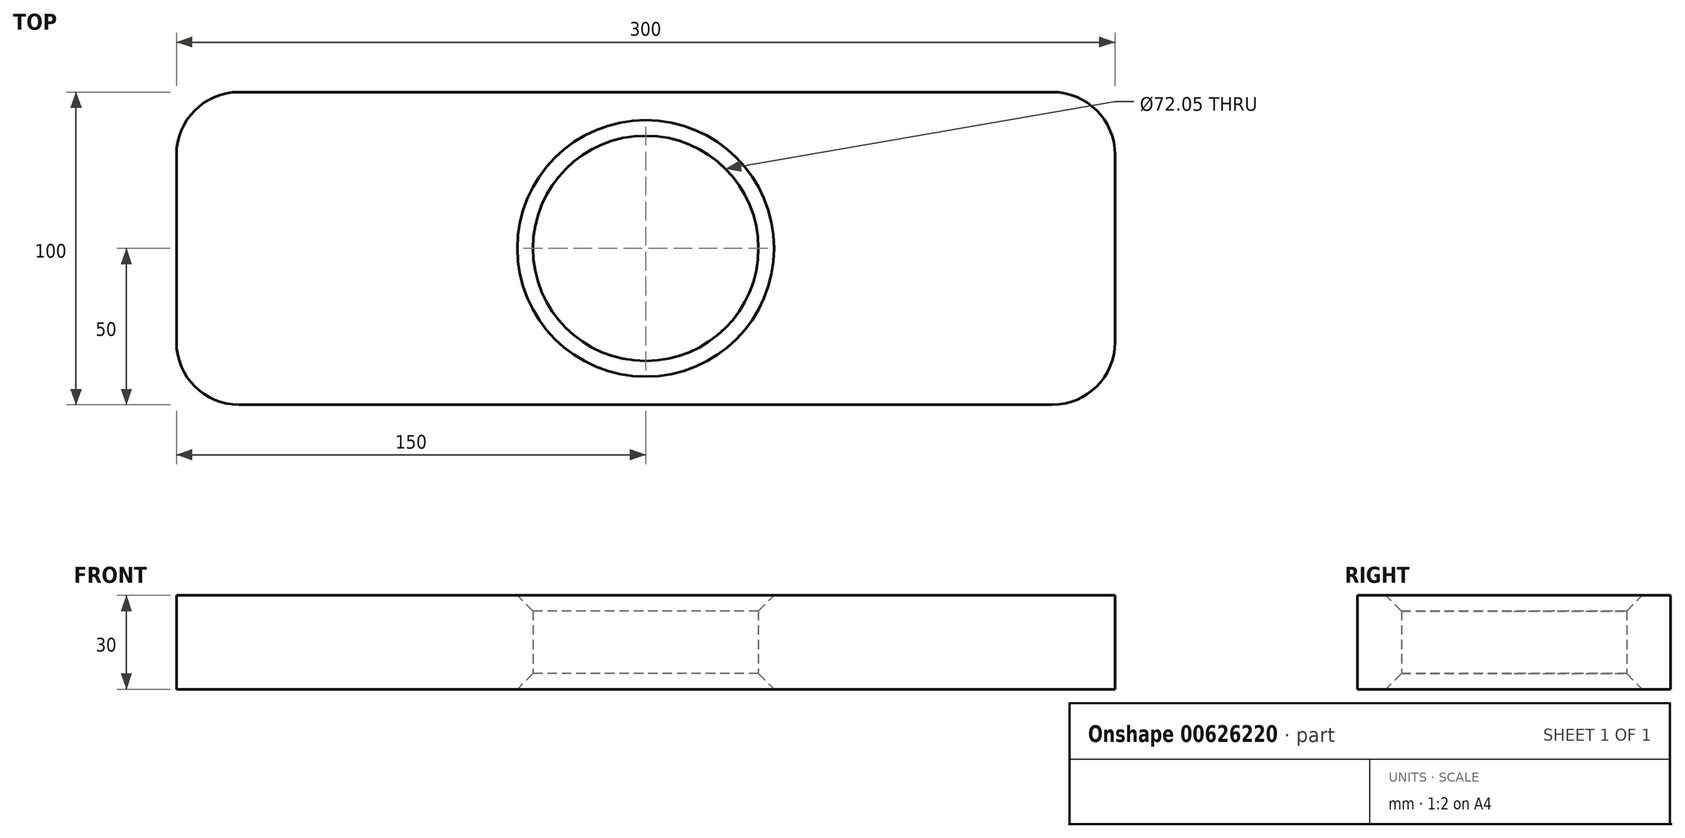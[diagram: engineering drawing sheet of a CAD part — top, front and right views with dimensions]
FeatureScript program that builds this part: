
annotation { "Feature Type Name" : "Feature", "Feature Type Description" : "" }
export const myFeature = defineFeature(function(context is Context, id is Id, definition is map)
    precondition{}
    {
        {
            var Q0;
            Q0=qCreatedBy(makeId("Top.planeOp"),FACE);
            var sketch = newSketch(context, id + "F0", { "sketchPlane" : qUnion([Q0])});
            skLineSegment(sketch, "E0.bottom", {"start": v(150, 50) * mm, "end": v(-150, 50) * mm});
            skLineSegment(sketch, "E0.top", {"start": v(150, -50) * mm, "end": v(-150, -50) * mm});
            skLineSegment(sketch, "E0.left", {"start": v(150, 50) * mm, "end": v(150, -50) * mm});
            skLineSegment(sketch, "E0.right", {"start": v(-150, 50) * mm, "end": v(-150, -50) * mm});
            skPoint(sketch, "E0.middle", {"position": v(0, 0) * mm});
            skCircle(sketch, "E1", {"center": v(0, 0) * mm, "radius": 36.02 * mm});
            skSolve(sketch);
        }
        {
            var Q0;
            Q0 = qSketchRegion(id + "F0", true);
            extrude(context, id + "F1", {"entities" : qUnion([Q0]), "depth" : 30 * mm, "offsetDistance" : 25 * mm});
        }
        {
            var Q0;
            Q0=makeQuery(id+"F1.opExtrude","SWEPT_EDGE",EDGE,{"disambiguationData":[OSD([sQuery(id+"F0.wireOp",EDGE,"E0.top"),sQuery(id+"F0.wireOp",EDGE,"E0.left")])]});
            var Q1;
            Q1=makeQuery(id+"F1.opExtrude","SWEPT_EDGE",EDGE,{"disambiguationData":[OSD([sQuery(id+"F0.wireOp",EDGE,"E0.bottom"),sQuery(id+"F0.wireOp",EDGE,"E0.left")])]});
            var Q2;
            Q2=makeQuery(id+"F1.opExtrude","SWEPT_EDGE",EDGE,{"disambiguationData":[OSD([sQuery(id+"F0.wireOp",EDGE,"E0.top"),sQuery(id+"F0.wireOp",EDGE,"E0.right")])]});
            var Q3;
            Q3=makeQuery(id+"F1.opExtrude","SWEPT_EDGE",EDGE,{"disambiguationData":[OSD([sQuery(id+"F0.wireOp",EDGE,"E0.bottom"),sQuery(id+"F0.wireOp",EDGE,"E0.right")])]});
            fillet(context, id + "F2", {"entities" : qUnion([Q0, Q1, Q2, Q3]), "radius" : 20 * mm, "tangentPropagation" : true, "allowEdgeOverflow" : false});
        }
        {
            var Q0;
            Q0=makeQuery(id+"F1.opExtrude","CAP_EDGE",EDGE,{"disambiguationData":[OSD([sQuery(id+"F0.wireOp",EDGE,"E1")])],"isStart":false});
            var Q1;
            Q1=makeQuery(id+"F1.opExtrude","CAP_EDGE",EDGE,{"disambiguationData":[OSD([sQuery(id+"F0.wireOp",EDGE,"E1")])],"isStart":true});
            chamfer(context, id + "F3", {"entities" : qUnion([Q0, Q1]), "width" : 5 * mm, "tangentPropagation" : true});
        }
    });
